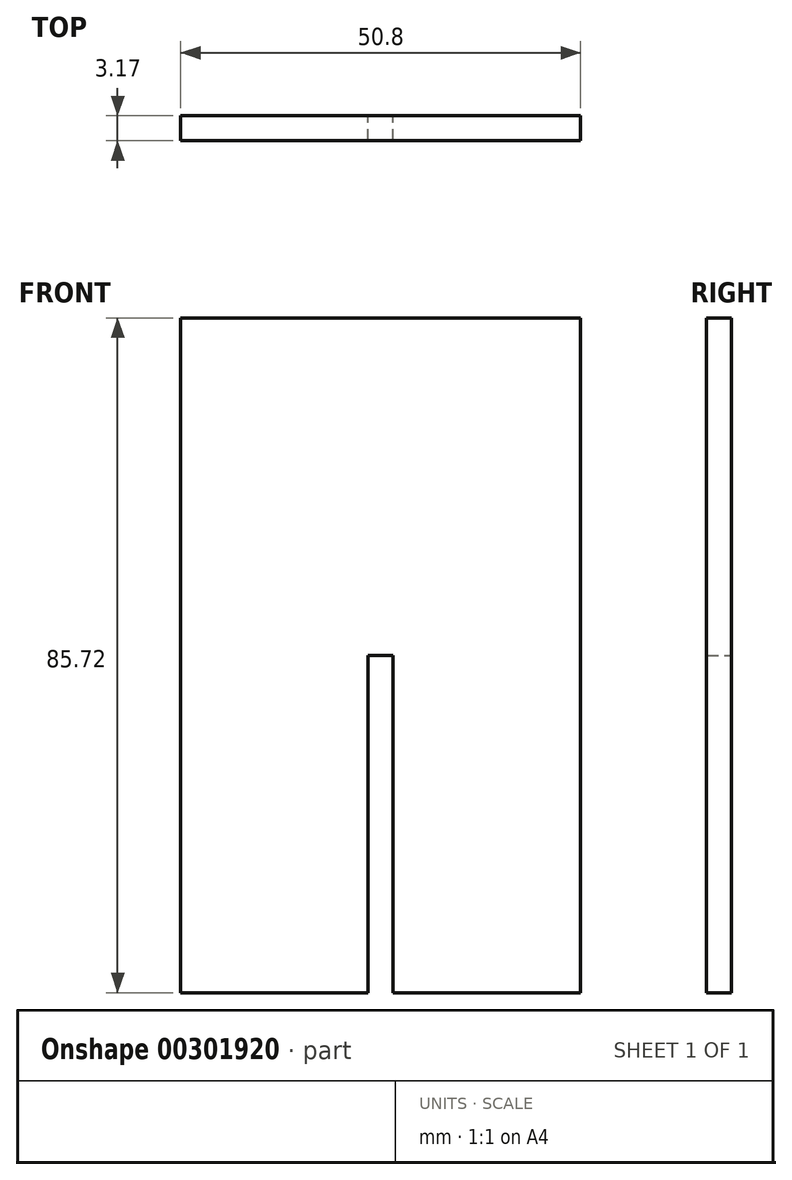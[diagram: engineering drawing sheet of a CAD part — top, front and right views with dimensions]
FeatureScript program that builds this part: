
annotation { "Feature Type Name" : "Feature", "Feature Type Description" : "" }
export const myFeature = defineFeature(function(context is Context, id is Id, definition is map)
    precondition{}
    {
        {
            var Q0;
            Q0=qCreatedBy(makeId("Front.planeOp"),FACE);
            var sketch = newSketch(context, id + "F0", { "sketchPlane" : qUnion([Q0])});
            skLineSegment(sketch, "E0.bottom", {"start": v(25.4, -42.86) * mm, "end": v(-25.4, -42.86) * mm});
            skLineSegment(sketch, "E0.top", {"start": v(25.4, 42.86) * mm, "end": v(-25.4, 42.86) * mm});
            skLineSegment(sketch, "E0.left", {"start": v(25.4, -42.86) * mm, "end": v(25.4, 42.86) * mm});
            skLineSegment(sketch, "E0.right", {"start": v(-25.4, -42.86) * mm, "end": v(-25.4, 42.86) * mm});
            skPoint(sketch, "E0.middle", {"position": v(0, 0) * mm});
            skLineSegment(sketch, "E1.bottom", {"start": v(-1.59, -42.86) * mm, "end": v(1.59, -42.86) * mm});
            skLineSegment(sketch, "E1.top", {"start": v(-1.59, 0) * mm, "end": v(1.59, 0) * mm});
            skLineSegment(sketch, "E1.left", {"start": v(-1.59, -42.86) * mm, "end": v(-1.59, 0) * mm});
            skLineSegment(sketch, "E1.right", {"start": v(1.59, -42.86) * mm, "end": v(1.59, 0) * mm});
            skSolve(sketch);
        }
        {
            var Q0;
            Q0=makeQuery(id+"F0.imprint","IMPRINT",FACE,{"disambiguationData":[TD([[makeQuery(id+"F0.imprint","IMPRINT",EDGE,{"derivedFrom":sQuery(id+"F0.wireOp",EDGE,"E0.top")}),1.0]])]});
            extrude(context, id + "F1", {"entities" : qUnion([Q0]), "depth" : 3.17 * mm});
        }
    });
